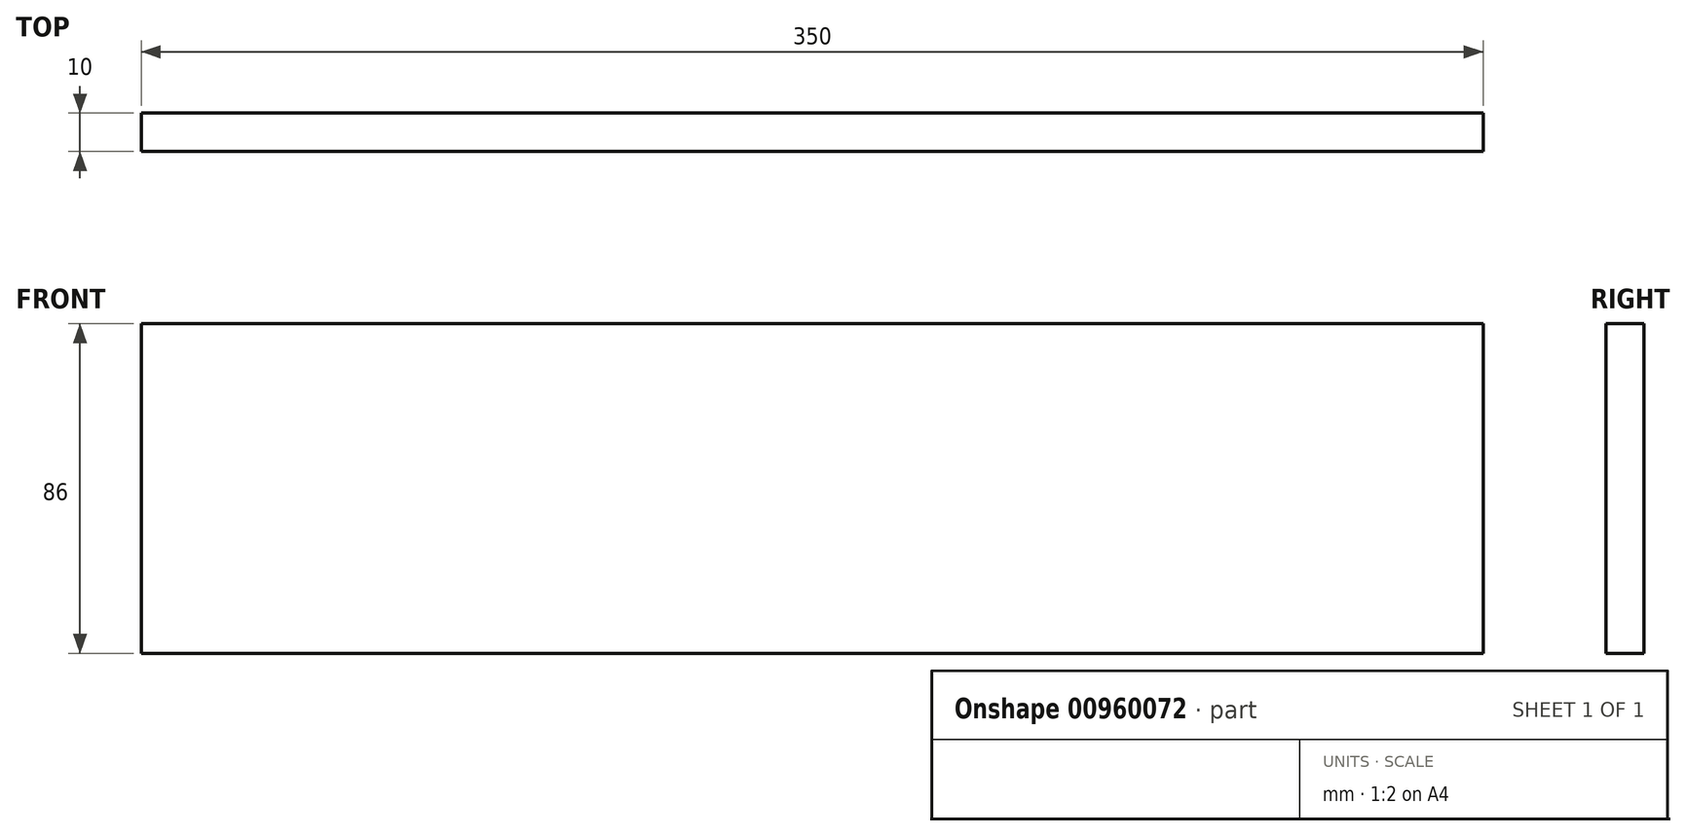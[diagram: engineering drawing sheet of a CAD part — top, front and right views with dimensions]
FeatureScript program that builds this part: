
annotation { "Feature Type Name" : "Feature", "Feature Type Description" : "" }
export const myFeature = defineFeature(function(context is Context, id is Id, definition is map)
    precondition{}
    {
        {
            var Q0;
            Q0=qCreatedBy(makeId("Front.planeOp"),FACE);
            var sketch = newSketch(context, id + "F0", { "sketchPlane" : qUnion([Q0])});
            skLineSegment(sketch, "E0.bottom", {"start": v(175, 43) * mm, "end": v(-175, 43) * mm});
            skLineSegment(sketch, "E0.top", {"start": v(175, -43) * mm, "end": v(-175, -43) * mm});
            skLineSegment(sketch, "E0.left", {"start": v(175, 43) * mm, "end": v(175, -43) * mm});
            skLineSegment(sketch, "E0.right", {"start": v(-175, 43) * mm, "end": v(-175, -43) * mm});
            skPoint(sketch, "E0.middle", {"position": v(0, 0) * mm});
            skSolve(sketch);
        }
        {
            var Q0;
            Q0 = qSketchRegion(id + "F0", true);
            extrude(context, id + "F1", {"entities" : qUnion([Q0]), "depth" : 10 * mm, "offsetDistance" : 25 * mm});
        }
    });
